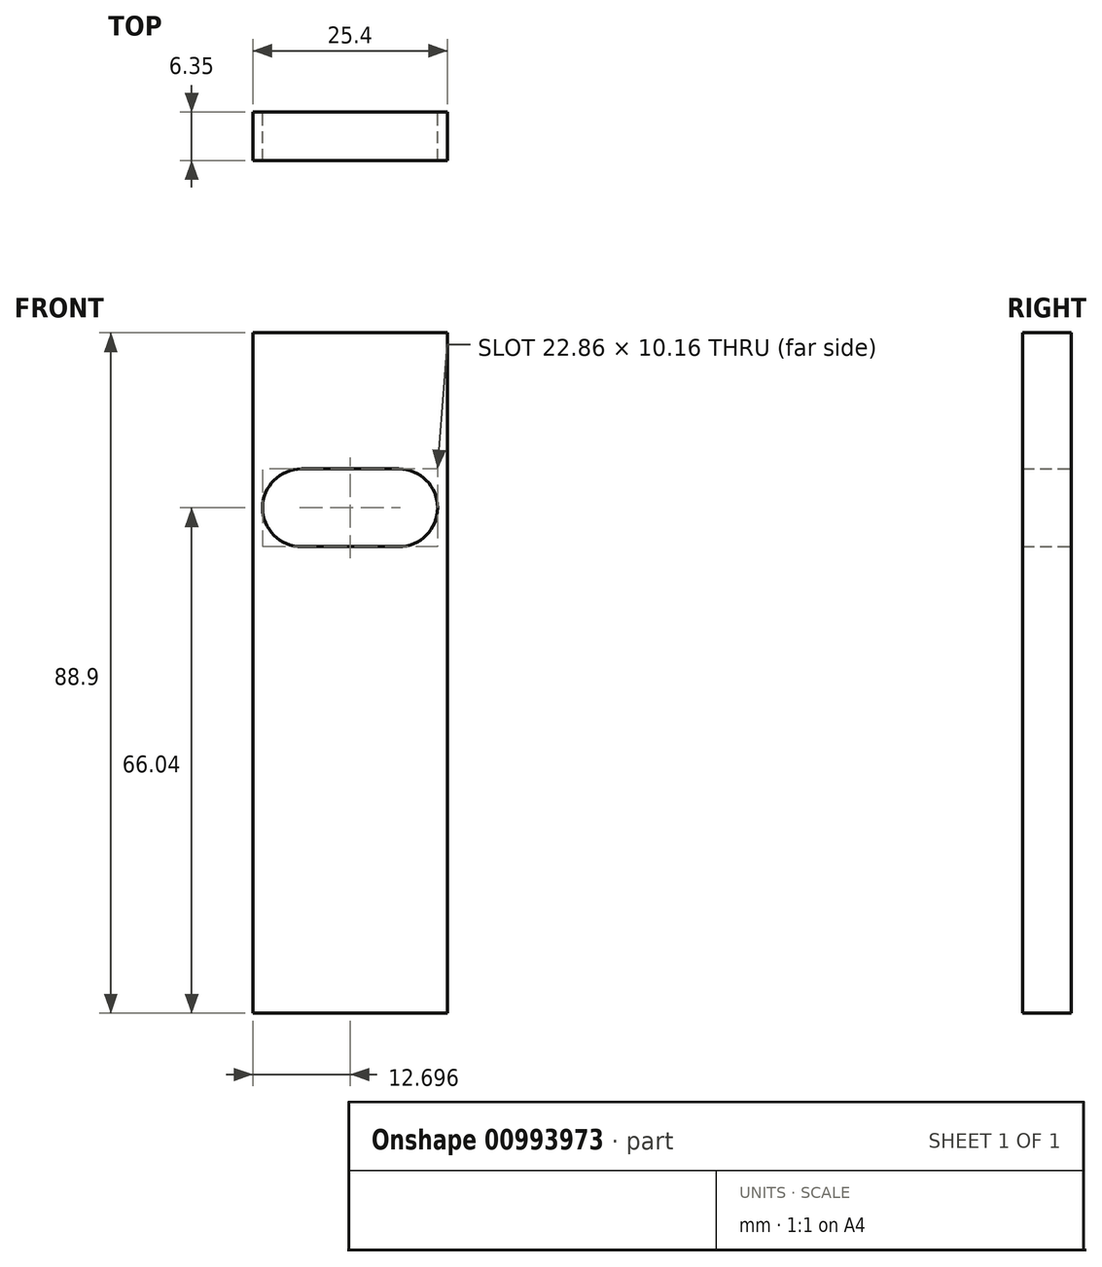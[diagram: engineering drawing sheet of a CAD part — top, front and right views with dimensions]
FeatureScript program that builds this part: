
annotation { "Feature Type Name" : "Feature", "Feature Type Description" : "" }
export const myFeature = defineFeature(function(context is Context, id is Id, definition is map)
    precondition{}
    {
        {
            var Q0;
            Q0=qCreatedBy(makeId("Top.planeOp"),FACE);
            var sketch = newSketch(context, id + "F0", { "sketchPlane" : qUnion([Q0])});
            skLineSegment(sketch, "E0.bottom", {"start": v(-7.8, 25.06) * mm, "end": v(17.6, 25.06) * mm});
            skLineSegment(sketch, "E0.top", {"start": v(-7.8, -38.44) * mm, "end": v(17.6, -38.44) * mm});
            skLineSegment(sketch, "E0.left", {"start": v(-7.8, 25.06) * mm, "end": v(-7.8, -38.44) * mm});
            skLineSegment(sketch, "E0.right", {"start": v(17.6, 25.06) * mm, "end": v(17.6, -38.44) * mm});
            skSolve(sketch);
        }
        {
            var Q0;
            Q0=makeQuery(id+"F0.imprint","IMPRINT",FACE,{"disambiguationData":[TD([[makeQuery(id+"F0.imprint","IMPRINT",EDGE,{"derivedFrom":sQuery(id+"F0.wireOp",EDGE,"E0.bottom")}),-1.0]])]});
            extrude(context, id + "F1", {"entities" : qUnion([Q0]), "depth" : 6.35 * mm, "offsetDistance" : 25.4 * mm});
        }
        {
            var Q0;
            Q0=makeQuery(id+"F1.opExtrude","CAP_FACE",FACE,{"disambiguationData":[OSD([sQuery(id+"F0.wireOp",EDGE,"E0.bottom"),sQuery(id+"F0.wireOp",EDGE,"E0.top"),sQuery(id+"F0.wireOp",EDGE,"E0.left"),sQuery(id+"F0.wireOp",EDGE,"E0.right")])],"isStart":true});
            var sketch = newSketch(context, id + "F2", { "sketchPlane" : qUnion([Q0])});
            skLineSegment(sketch, "E1.bottom", {"start": v(17.6, -25.06) * mm, "end": v(-7.8, -25.06) * mm});
            skLineSegment(sketch, "E1.top", {"start": v(17.6, -18.71) * mm, "end": v(-7.8, -18.71) * mm});
            skLineSegment(sketch, "E1.left", {"start": v(17.6, -25.06) * mm, "end": v(17.6, -18.71) * mm});
            skLineSegment(sketch, "E1.right", {"start": v(-7.8, -25.06) * mm, "end": v(-7.8, -18.71) * mm});
            skSolve(sketch);
        }
        {
            var Q0;
            Q0=makeQuery(id+"F2.imprint","IMPRINT",FACE,{"disambiguationData":[TD([[makeQuery(id+"F2.imprint","IMPRINT",EDGE,{"derivedFrom":sQuery(id+"F2.wireOp",EDGE,"E1.bottom")}),1.0]])]});
            extrude(context, id + "F3", {"entities" : qUnion([Q0]), "operationType" : NewBodyOperationType.ADD, "depth" : 82.55 * mm, "offsetDistance" : 25.4 * mm});
        }
        {
            var Q0;
            Q0=makeQuery(id+"F3.boolean.opBoolean","MERGE",FACE,{"derivedFrom":[makeQuery(id+"F1.opExtrude","SWEPT_FACE",FACE,{"disambiguationData":[OSD([sQuery(id+"F0.wireOp",EDGE,"E0.bottom")])]}),makeQuery(id+"F3.opExtrude","SWEPT_FACE",FACE,{"disambiguationData":[OSD([sQuery(id+"F2.wireOp",EDGE,"E1.bottom")])]})]});
            var sketch = newSketch(context, id + "F4", { "sketchPlane" : qUnion([Q0])});
            skLineSegment(sketch, "E2.bottom", {"start": v(-17.6, 6.35) * mm, "end": v(7.8, 6.35) * mm});
            skLineSegment(sketch, "E2.top", {"start": v(-17.6, -11.43) * mm, "end": v(7.8, -11.43) * mm});
            skLineSegment(sketch, "E2.left", {"start": v(-17.6, 6.35) * mm, "end": v(-17.6, -11.43) * mm});
            skLineSegment(sketch, "E2.right", {"start": v(7.8, 6.35) * mm, "end": v(7.8, -11.43) * mm});
            skLineSegment(sketch, "E3.bottom", {"start": v(7.8, -11.43) * mm, "end": v(-17.6, -11.43) * mm});
            skLineSegment(sketch, "E3.top", {"start": v(7.8, -21.59) * mm, "end": v(-17.6, -21.59) * mm});
            skLineSegment(sketch, "E3.left", {"start": v(7.8, -11.43) * mm, "end": v(7.8, -21.59) * mm});
            skLineSegment(sketch, "E3.right", {"start": v(-17.6, -11.43) * mm, "end": v(-17.6, -21.59) * mm});
            skLineSegment(sketch, "E4.top", {"start": v(7.8, -54.61) * mm, "end": v(-17.6, -54.61) * mm});
            skLineSegment(sketch, "E4.left", {"start": v(7.8, -21.59) * mm, "end": v(7.8, -54.61) * mm});
            skLineSegment(sketch, "E4.right", {"start": v(-17.6, -21.59) * mm, "end": v(-17.6, -54.61) * mm});
            skLineSegment(sketch, "E5.top", {"start": v(7.8, -64.77) * mm, "end": v(-17.6, -64.77) * mm});
            skLineSegment(sketch, "E5.left", {"start": v(7.8, -54.61) * mm, "end": v(7.8, -64.77) * mm});
            skLineSegment(sketch, "E5.right", {"start": v(-17.6, -54.61) * mm, "end": v(-17.6, -64.77) * mm});
            skLineSegment(sketch, "E6.top", {"start": v(7.8, -82.55) * mm, "end": v(-17.6, -82.55) * mm});
            skLineSegment(sketch, "E6.left", {"start": v(7.8, -64.77) * mm, "end": v(7.8, -82.55) * mm});
            skLineSegment(sketch, "E6.right", {"start": v(-17.6, -64.77) * mm, "end": v(-17.6, -82.55) * mm});
            skLineSegment(sketch, "E7", {"start": v(7.8, -16.5) * mm, "end": v(-17.6, -16.5) * mm});
            skLineSegment(sketch, "E8.bottom", {"start": v(-17.6, -59.7) * mm, "end": v(7.8, -59.7) * mm});
            skLineSegment(sketch, "E8.top", {"start": v(-17.6, -59.7) * mm, "end": v(7.8, -59.7) * mm});
            skLineSegment(sketch, "E8.left", {"start": v(-17.6, -59.7) * mm, "end": v(-17.6, -59.7) * mm});
            skLineSegment(sketch, "E8.right", {"start": v(7.8, -59.69) * mm, "end": v(7.8, -59.7) * mm});
            skLineSegment(sketch, "E9.bottom", {"start": v(-17.6, 6.35) * mm, "end": v(-11.26, 6.35) * mm});
            skLineSegment(sketch, "E9.top", {"start": v(-17.6, -82.55) * mm, "end": v(-11.26, -82.55) * mm});
            skLineSegment(sketch, "E9.left", {"start": v(-17.6, 6.35) * mm, "end": v(-17.6, -82.55) * mm});
            skLineSegment(sketch, "E9.right", {"start": v(-11.26, 6.35) * mm, "end": v(-11.26, -82.55) * mm});
            skLineSegment(sketch, "E10.bottom", {"start": v(7.8, -82.55) * mm, "end": v(1.44, -82.55) * mm});
            skLineSegment(sketch, "E10.top", {"start": v(7.8, 6.35) * mm, "end": v(1.44, 6.35) * mm});
            skLineSegment(sketch, "E10.left", {"start": v(7.8, -82.55) * mm, "end": v(7.8, 6.35) * mm});
            skLineSegment(sketch, "E10.right", {"start": v(1.44, -82.55) * mm, "end": v(1.44, 6.35) * mm});
            skCircle(sketch, "E11", {"center": v(1.44, -59.7) * mm, "radius": 5.08 * mm});
            skCircle(sketch, "E12", {"center": v(-11.26, -59.7) * mm, "radius": 5.08 * mm});
            skCircle(sketch, "E13", {"center": v(-11.26, -16.5) * mm, "radius": 5.08 * mm});
            skCircle(sketch, "E14", {"center": v(1.44, -16.5) * mm, "radius": 5.08 * mm});
            skSolve(sketch);
        }
        {
            var Q0;
            {var subQ0=sQuery(id+"F4.wireOp",EDGE,"E13");var subQ1=sQuery(id+"F4.wireOp",EDGE,"E7");var subQ2=makeQuery(id+"F4.imprint","INTERSECT",VERTEX,{"disambiguationData":[OD(0.0)],"derivedFrom":[subQ1,subQ0]});Q0=makeQuery(id+"F4.imprint","IMPRINT",FACE,{"disambiguationData":[TD([[makeQuery(id+"F4.imprint","IMPRINT",EDGE,{"disambiguationData":[TD([[subQ2,-1.0]])],"derivedFrom":subQ1}),1.0]])]});}
            var Q1;
            {var subQ0=sQuery(id+"F4.wireOp",EDGE,"E9.right");var subQ1=sQuery(id+"F4.wireOp",EDGE,"E7");var subQ2=makeQuery(id+"F4.imprint","INTERSECT",VERTEX,{"derivedFrom":[subQ1,subQ0]});Q1=makeQuery(id+"F4.imprint","IMPRINT",FACE,{"disambiguationData":[TD([[makeQuery(id+"F4.imprint","IMPRINT",EDGE,{"disambiguationData":[TD([[subQ2,-1.0]])],"derivedFrom":subQ1}),1.0]])]});}
            var Q2;
            {var subQ0=sQuery(id+"F4.wireOp",EDGE,"E9.right");var subQ1=sQuery(id+"F4.wireOp",EDGE,"E7");var subQ2=makeQuery(id+"F4.imprint","INTERSECT",VERTEX,{"derivedFrom":[subQ1,subQ0]});Q2=makeQuery(id+"F4.imprint","IMPRINT",FACE,{"disambiguationData":[TD([[makeQuery(id+"F4.imprint","IMPRINT",EDGE,{"disambiguationData":[TD([[subQ2,-1.0]])],"derivedFrom":subQ1}),-1.0]])]});}
            var Q3;
            {var subQ0=sQuery(id+"F4.wireOp",EDGE,"E14");var subQ5=sQuery(id+"F4.wireOp",EDGE,"E7");var subQ6=makeQuery(id+"F4.imprint","INTERSECT",VERTEX,{"disambiguationData":[OD(1.0)],"derivedFrom":[subQ5,subQ0]});Q3=makeQuery(id+"F4.imprint","IMPRINT",FACE,{"disambiguationData":[TD([[makeQuery(id+"F4.imprint","IMPRINT",EDGE,{"disambiguationData":[TD([[subQ6,-1.0]])],"derivedFrom":subQ5}),-1.0]])]});}
            var Q4;
            {var subQ0=sQuery(id+"F4.wireOp",EDGE,"E10.right");var subQ1=sQuery(id+"F4.wireOp",EDGE,"E7");var subQ2=makeQuery(id+"F4.imprint","INTERSECT",VERTEX,{"derivedFrom":[subQ1,subQ0]});Q4=makeQuery(id+"F4.imprint","IMPRINT",FACE,{"disambiguationData":[TD([[makeQuery(id+"F4.imprint","IMPRINT",EDGE,{"disambiguationData":[TD([[subQ2,-1.0]])],"derivedFrom":subQ1}),-1.0]])]});}
            var Q5;
            {var subQ0=sQuery(id+"F4.wireOp",EDGE,"E14");var subQ1=sQuery(id+"F4.wireOp",EDGE,"E7");var subQ2=makeQuery(id+"F4.imprint","INTERSECT",VERTEX,{"disambiguationData":[OD(0.0)],"derivedFrom":[subQ1,subQ0]});Q5=makeQuery(id+"F4.imprint","IMPRINT",FACE,{"disambiguationData":[TD([[makeQuery(id+"F4.imprint","IMPRINT",EDGE,{"disambiguationData":[TD([[subQ2,-1.0]])],"derivedFrom":subQ1}),-1.0]])]});}
            var Q6;
            {var subQ0=sQuery(id+"F4.wireOp",EDGE,"E14");var subQ1=sQuery(id+"F4.wireOp",EDGE,"E7");var subQ2=makeQuery(id+"F4.imprint","INTERSECT",VERTEX,{"disambiguationData":[OD(0.0)],"derivedFrom":[subQ1,subQ0]});Q6=makeQuery(id+"F4.imprint","IMPRINT",FACE,{"disambiguationData":[TD([[makeQuery(id+"F4.imprint","IMPRINT",EDGE,{"disambiguationData":[TD([[subQ2,-1.0]])],"derivedFrom":subQ1}),1.0]])]});}
            var Q7;
            {var subQ0=sQuery(id+"F4.wireOp",EDGE,"E14");var subQ5=sQuery(id+"F4.wireOp",EDGE,"E7");var subQ6=makeQuery(id+"F4.imprint","INTERSECT",VERTEX,{"disambiguationData":[OD(1.0)],"derivedFrom":[subQ5,subQ0]});Q7=makeQuery(id+"F4.imprint","IMPRINT",FACE,{"disambiguationData":[TD([[makeQuery(id+"F4.imprint","IMPRINT",EDGE,{"disambiguationData":[TD([[subQ6,-1.0]])],"derivedFrom":subQ5}),1.0]])]});}
            var Q8;
            {var subQ0=sQuery(id+"F4.wireOp",EDGE,"E10.right");var subQ1=sQuery(id+"F4.wireOp",EDGE,"E7");var subQ2=makeQuery(id+"F4.imprint","INTERSECT",VERTEX,{"derivedFrom":[subQ1,subQ0]});Q8=makeQuery(id+"F4.imprint","IMPRINT",FACE,{"disambiguationData":[TD([[makeQuery(id+"F4.imprint","IMPRINT",EDGE,{"disambiguationData":[TD([[subQ2,-1.0]])],"derivedFrom":subQ1}),1.0]])]});}
            var Q9;
            {var subQ0=sQuery(id+"F4.wireOp",EDGE,"E13");var subQ1=sQuery(id+"F4.wireOp",EDGE,"E7");var subQ2=makeQuery(id+"F4.imprint","INTERSECT",VERTEX,{"disambiguationData":[OD(0.0)],"derivedFrom":[subQ1,subQ0]});Q9=makeQuery(id+"F4.imprint","IMPRINT",FACE,{"disambiguationData":[TD([[makeQuery(id+"F4.imprint","IMPRINT",EDGE,{"disambiguationData":[TD([[subQ2,-1.0]])],"derivedFrom":subQ1}),-1.0]])]});}
            var Q10;
            {var subQ0=sQuery(id+"F4.wireOp",EDGE,"E12");var subQ1=sQuery(id+"F4.wireOp",EDGE,"E8.top");var subQ2=makeQuery(id+"F4.imprint","INTERSECT",VERTEX,{"disambiguationData":[OD(0.0)],"derivedFrom":[subQ1,subQ0]});Q10=makeQuery(id+"F4.imprint","IMPRINT",FACE,{"disambiguationData":[TD([[makeQuery(id+"F4.imprint","IMPRINT",EDGE,{"disambiguationData":[TD([[subQ2,-1.0]])],"derivedFrom":subQ1}),1.0]])]});}
            var Q11;
            {var subQ0=sQuery(id+"F4.wireOp",EDGE,"E9.right");var subQ1=sQuery(id+"F4.wireOp",EDGE,"E8.top");var subQ2=makeQuery(id+"F4.imprint","INTERSECT",VERTEX,{"derivedFrom":[subQ1,subQ0]});Q11=makeQuery(id+"F4.imprint","IMPRINT",FACE,{"disambiguationData":[TD([[makeQuery(id+"F4.imprint","IMPRINT",EDGE,{"disambiguationData":[TD([[subQ2,-1.0]])],"derivedFrom":subQ1}),1.0]])]});}
            var Q12;
            {var subQ0=sQuery(id+"F4.wireOp",EDGE,"E9.right");var subQ1=sQuery(id+"F4.wireOp",EDGE,"E8.top");var subQ2=makeQuery(id+"F4.imprint","INTERSECT",VERTEX,{"derivedFrom":[subQ1,subQ0]});Q12=makeQuery(id+"F4.imprint","IMPRINT",FACE,{"disambiguationData":[TD([[makeQuery(id+"F4.imprint","IMPRINT",EDGE,{"disambiguationData":[TD([[subQ2,-1.0]])],"derivedFrom":subQ1}),-1.0]])]});}
            var Q13;
            {var subQ0=sQuery(id+"F4.wireOp",EDGE,"E12");var subQ1=sQuery(id+"F4.wireOp",EDGE,"E8.top");var subQ2=makeQuery(id+"F4.imprint","INTERSECT",VERTEX,{"disambiguationData":[OD(0.0)],"derivedFrom":[subQ1,subQ0]});Q13=makeQuery(id+"F4.imprint","IMPRINT",FACE,{"disambiguationData":[TD([[makeQuery(id+"F4.imprint","IMPRINT",EDGE,{"disambiguationData":[TD([[subQ2,-1.0]])],"derivedFrom":subQ1}),-1.0]])]});}
            var Q14;
            {var subQ3=sQuery(id+"F4.wireOp",EDGE,"E12");var subQ5=sQuery(id+"F4.wireOp",EDGE,"E8.top");var subQ6=makeQuery(id+"F4.imprint","INTERSECT",VERTEX,{"disambiguationData":[OD(1.0)],"derivedFrom":[subQ5,subQ3]});Q14=makeQuery(id+"F4.imprint","IMPRINT",FACE,{"disambiguationData":[TD([[makeQuery(id+"F4.imprint","IMPRINT",EDGE,{"disambiguationData":[TD([[subQ6,-1.0]])],"derivedFrom":subQ5}),1.0]])]});}
            var Q15;
            {var subQ0=sQuery(id+"F4.wireOp",EDGE,"E11");var subQ1=sQuery(id+"F4.wireOp",EDGE,"E8.top");var subQ2=makeQuery(id+"F4.imprint","INTERSECT",VERTEX,{"disambiguationData":[OD(0.0)],"derivedFrom":[subQ1,subQ0]});Q15=makeQuery(id+"F4.imprint","IMPRINT",FACE,{"disambiguationData":[TD([[makeQuery(id+"F4.imprint","IMPRINT",EDGE,{"disambiguationData":[TD([[subQ2,-1.0]])],"derivedFrom":subQ1}),1.0]])]});}
            var Q16;
            {var subQ0=sQuery(id+"F4.wireOp",EDGE,"E11");var subQ1=sQuery(id+"F4.wireOp",EDGE,"E8.top");var subQ2=makeQuery(id+"F4.imprint","INTERSECT",VERTEX,{"disambiguationData":[OD(0.0)],"derivedFrom":[subQ1,subQ0]});Q16=makeQuery(id+"F4.imprint","IMPRINT",FACE,{"disambiguationData":[TD([[makeQuery(id+"F4.imprint","IMPRINT",EDGE,{"disambiguationData":[TD([[subQ2,-1.0]])],"derivedFrom":subQ1}),-1.0]])]});}
            var Q17;
            {var subQ3=sQuery(id+"F4.wireOp",EDGE,"E12");var subQ5=sQuery(id+"F4.wireOp",EDGE,"E8.top");var subQ6=makeQuery(id+"F4.imprint","INTERSECT",VERTEX,{"disambiguationData":[OD(1.0)],"derivedFrom":[subQ5,subQ3]});Q17=makeQuery(id+"F4.imprint","IMPRINT",FACE,{"disambiguationData":[TD([[makeQuery(id+"F4.imprint","IMPRINT",EDGE,{"disambiguationData":[TD([[subQ6,-1.0]])],"derivedFrom":subQ5}),-1.0]])]});}
            var Q18;
            {var subQ0=sQuery(id+"F4.wireOp",EDGE,"E10.right");var subQ1=sQuery(id+"F4.wireOp",EDGE,"E8.top");var subQ2=makeQuery(id+"F4.imprint","INTERSECT",VERTEX,{"derivedFrom":[subQ1,subQ0]});Q18=makeQuery(id+"F4.imprint","IMPRINT",FACE,{"disambiguationData":[TD([[makeQuery(id+"F4.imprint","IMPRINT",EDGE,{"disambiguationData":[TD([[subQ2,-1.0]])],"derivedFrom":subQ1}),1.0]])]});}
            var Q19;
            {var subQ0=sQuery(id+"F4.wireOp",EDGE,"E10.right");var subQ1=sQuery(id+"F4.wireOp",EDGE,"E8.top");var subQ2=makeQuery(id+"F4.imprint","INTERSECT",VERTEX,{"derivedFrom":[subQ1,subQ0]});Q19=makeQuery(id+"F4.imprint","IMPRINT",FACE,{"disambiguationData":[TD([[makeQuery(id+"F4.imprint","IMPRINT",EDGE,{"disambiguationData":[TD([[subQ2,-1.0]])],"derivedFrom":subQ1}),-1.0]])]});}
            extrude(context, id + "F5", {"entities" : qUnion([Q0, Q1, Q2, Q3, Q4, Q5, Q6, Q7, Q8, Q9, Q10, Q11, Q12, Q13, Q14, Q15, Q16, Q17, Q18, Q19]), "operationType" : NewBodyOperationType.REMOVE, "oppositeDirection" : true, "depth" : 25.4 * mm, "offsetDistance" : 25.4 * mm});
        }
        {
            var Q0;
            Q0=makeQuery(id+"F3.boolean.opBoolean","MERGE",FACE,{"derivedFrom":[makeQuery(id+"F1.opExtrude","SWEPT_FACE",FACE,{"disambiguationData":[OSD([sQuery(id+"F0.wireOp",EDGE,"E0.left")])]}),makeQuery(id+"F3.opExtrude","SWEPT_FACE",FACE,{"disambiguationData":[OSD([sQuery(id+"F2.wireOp",EDGE,"E1.right")])]})]});
            var sketch = newSketch(context, id + "F6", { "sketchPlane" : qUnion([Q0])});
            skLineSegment(sketch, "E15.bottom", {"start": v(-18.71, 0) * mm, "end": v(38.44, 0) * mm});
            skLineSegment(sketch, "E15.top", {"start": v(-18.71, 6.35) * mm, "end": v(38.44, 6.35) * mm});
            skLineSegment(sketch, "E15.left", {"start": v(-18.71, 0) * mm, "end": v(-18.71, 6.35) * mm});
            skLineSegment(sketch, "E15.right", {"start": v(38.44, 0) * mm, "end": v(38.44, 6.35) * mm});
            skSolve(sketch);
        }
        {
            var Q0;
            Q0=makeQuery(id+"F6.imprint","IMPRINT",FACE,{"disambiguationData":[TD([[makeQuery(id+"F6.imprint","IMPRINT",EDGE,{"derivedFrom":sQuery(id+"F6.wireOp",EDGE,"E15.bottom")}),1.0]])]});
            extrude(context, id + "F7", {"entities" : qUnion([Q0]), "operationType" : NewBodyOperationType.REMOVE, "oppositeDirection" : true, "depth" : 25.4 * mm, "offsetDistance" : 25.4 * mm});
        }
    });
